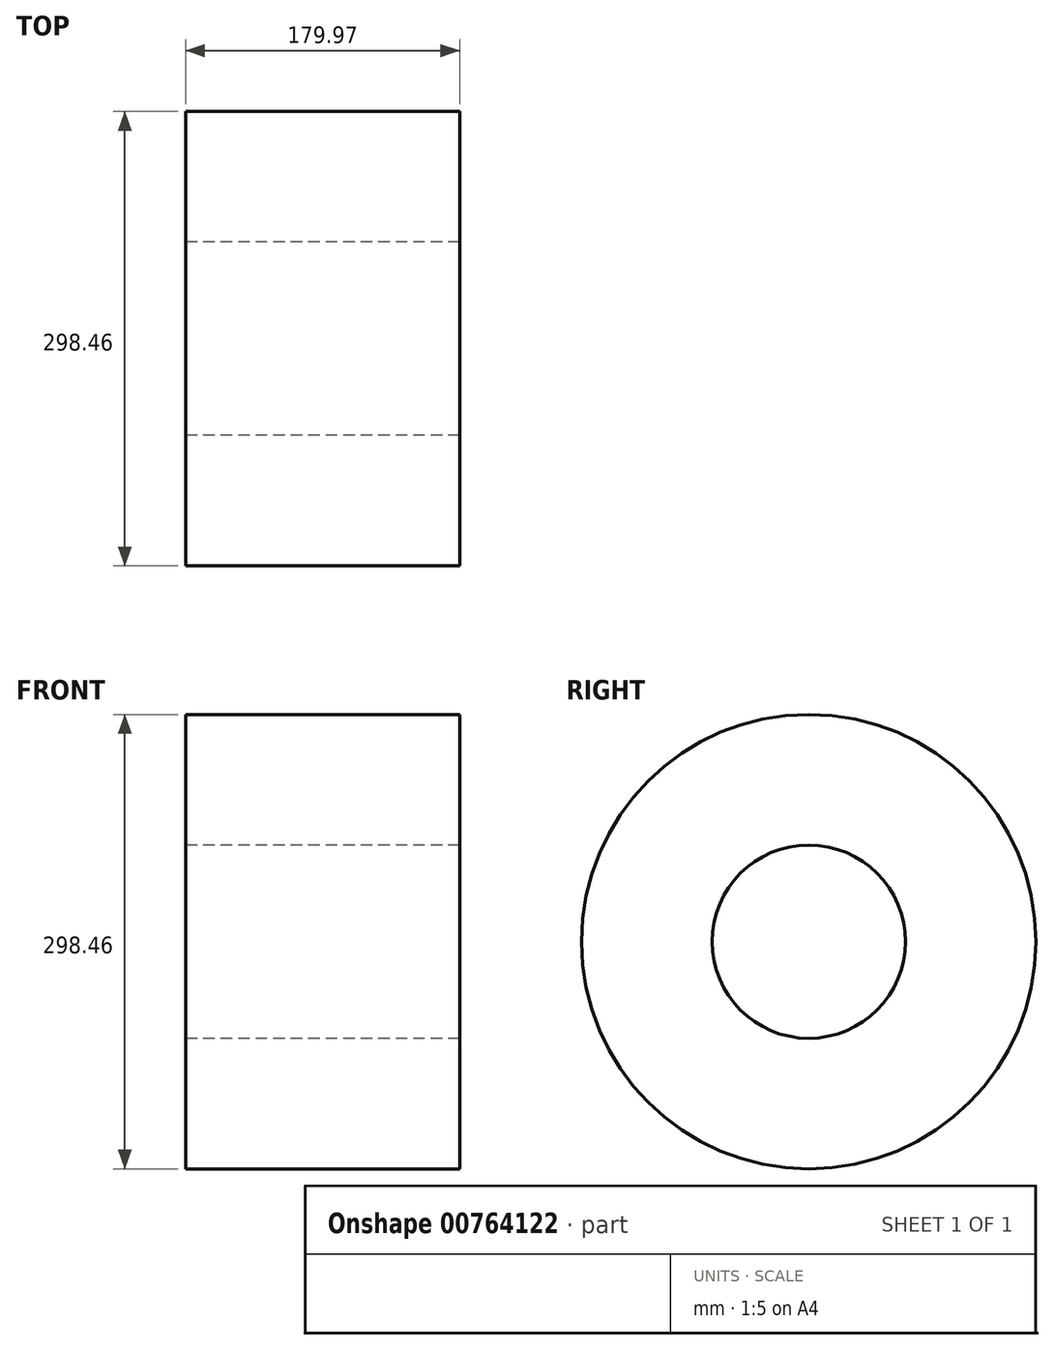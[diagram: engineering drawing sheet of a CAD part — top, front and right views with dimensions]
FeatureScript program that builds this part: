
annotation { "Feature Type Name" : "Feature", "Feature Type Description" : "" }
export const myFeature = defineFeature(function(context is Context, id is Id, definition is map)
    precondition{}
    {
        {
            var Q0;
            Q0=qCreatedBy(makeId("Front.planeOp"),FACE);
            var sketch = newSketch(context, id + "F0", { "sketchPlane" : qUnion([Q0])});
            skLineSegment(sketch, "E0", {"start": v(0, 0) * mm, "end": v(0, 149.23) * mm});
            skLineSegment(sketch, "E1", {"start": v(0, 149.23) * mm, "end": v(179.97, 149.23) * mm});
            skLineSegment(sketch, "E2", {"start": v(179.97, 149.23) * mm, "end": v(179.97, 0) * mm});
            skLineSegment(sketch, "E3", {"start": v(179.97, 0) * mm, "end": v(0, 0) * mm});
            skSolve(sketch);
        }
        {
            var Q0;
            Q0 = qSketchRegion(id + "F0", true);
            var Q1;
            Q1=sQuery(id+"F0.wireOp",EDGE,"E3");
            revolve(context, id + "F1", {"surfaceOperationType" : NewSurfaceOperationType.NEW, "entities" : qUnion([Q0]), "axis" : qUnion([Q1]), "revolveType" : RevolveType.FULL});
        }
        {
            var Q0;
            Q0=makeQuery(id+"F1.opRevolve","SWEPT_FACE",FACE,{"disambiguationData":[OSD([sQuery(id+"F0.wireOp",EDGE,"E0")])]});
            var sketch = newSketch(context, id + "F2", { "sketchPlane" : qUnion([Q0])});
            skSolve(sketch);
        }
        {
            var Q0;
            Q0=makeQuery(id+"F2.imprint","IMPRINT",FACE,{"disambiguationData":[TD([[makeQuery(id+"F2.imprint","IMPRINT",EDGE,{"derivedFrom":makeQuery(id+"F1.opRevolve","SWEPT_EDGE",EDGE,{"disambiguationData":[OSD([sQuery(id+"F0.wireOp",EDGE,"E0"),sQuery(id+"F0.wireOp",EDGE,"E1")])]})}),-1.0]])]});
            var sketch = newSketch(context, id + "F3", { "sketchPlane" : qUnion([Q0])});
            skCircle(sketch, "E4", {"center": v(0, 0) * mm, "radius": 63.5 * mm});
            skSolve(sketch);
        }
        {
            var Q0;
            Q0=sQuery(id+"F3.wireOp",VERTEX,"E4.center");
            var Q1;
            Q1=makeQuery(id+"F1.opRevolve","SWEPT_BODY",BODY,{"disambiguationData":[OSD([sQuery(id+"F0.wireOp",EDGE,"E0"),sQuery(id+"F0.wireOp",EDGE,"E1"),sQuery(id+"F0.wireOp",EDGE,"E2"),sQuery(id+"F0.wireOp",EDGE,"E3")])]});
            hole(context, id + "F4", {"style" : HoleStyle.SIMPLE, "endStyle" : HoleEndStyle.THROUGH, "holeDiameter" : 127 * mm, "majorDiameter" : 6.35 * mm, "isTappedThrough" : true, "tappedDepth" : 12.7 * mm, "tapClearance" : 3, "locations" : qUnion([Q0]), "scope" : qUnion([Q1])});
        }
    });
